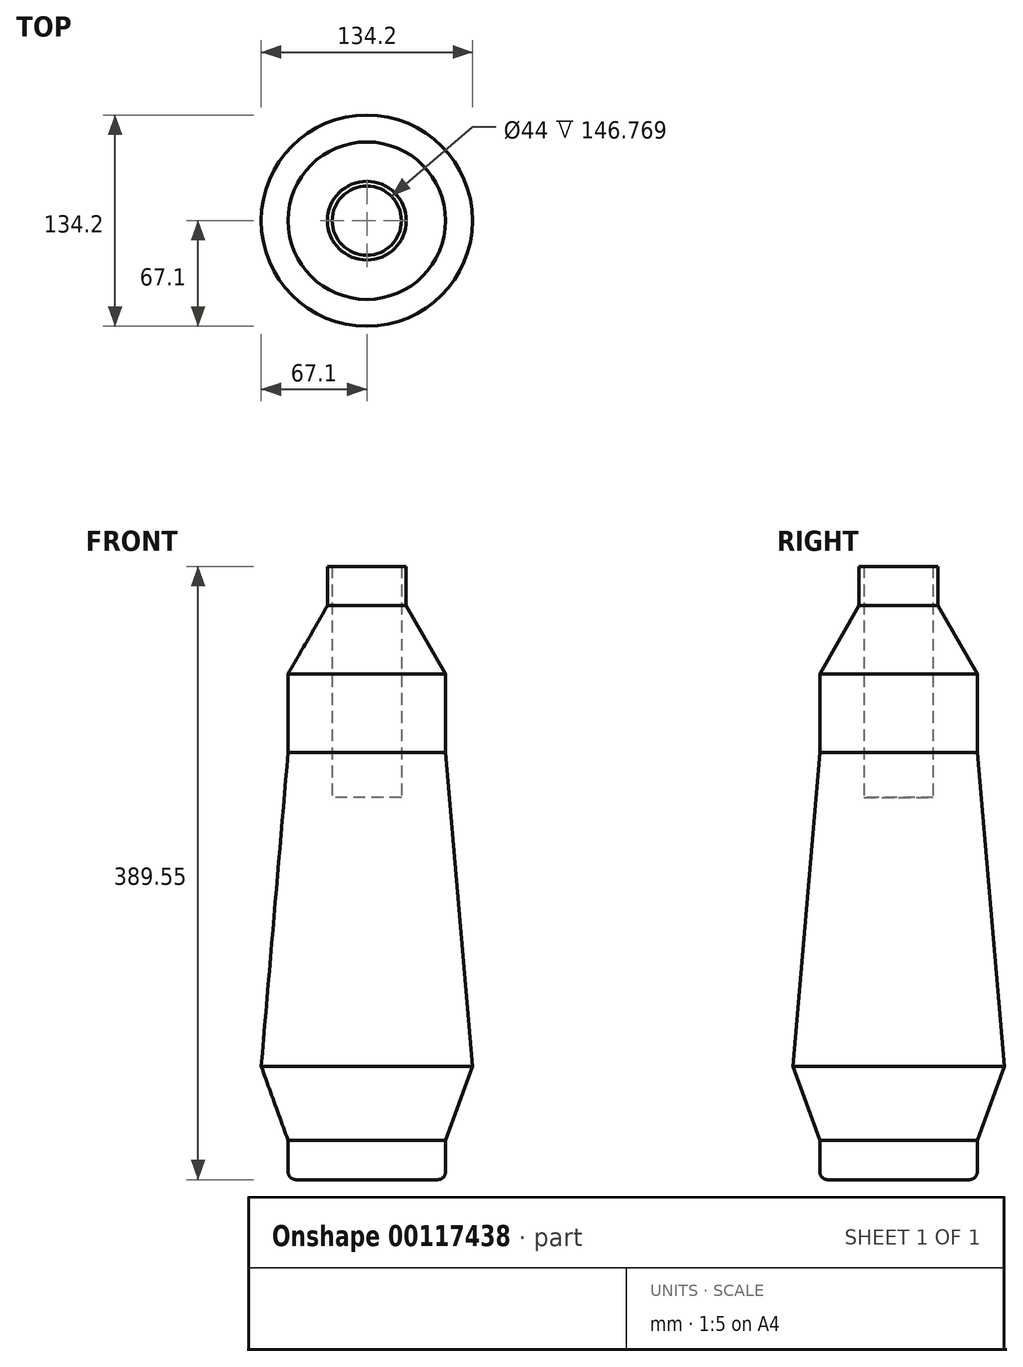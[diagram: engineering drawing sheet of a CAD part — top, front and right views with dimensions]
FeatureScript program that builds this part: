
annotation { "Feature Type Name" : "Feature", "Feature Type Description" : "" }
export const myFeature = defineFeature(function(context is Context, id is Id, definition is map)
    precondition{}
    {
        {
            var Q0;
            Q0=qCreatedBy(makeId("Front.planeOp"),FACE);
            var sketch = newSketch(context, id + "F0", { "sketchPlane" : qUnion([Q0])});
            skLineSegment(sketch, "E0", {"start": v(0, -242.78) * mm, "end": v(45, -242.78) * mm});
            skLineSegment(sketch, "E1", {"start": v(50, -237.78) * mm, "end": v(50, -217.78) * mm});
            skLineSegment(sketch, "E2", {"start": v(50, -217.78) * mm, "end": v(67.1, -170.8) * mm});
            skLineSegment(sketch, "E3", {"start": v(67.1, -170.8) * mm, "end": v(50, 28.47) * mm});
            skLineSegment(sketch, "E4", {"start": v(50, 28.47) * mm, "end": v(50, 78.47) * mm});
            skPoint(sketch, "E5.endSnap0", {"position": v(25, -242.78) * mm});
            skLineSegment(sketch, "E6", {"start": v(50, 78.47) * mm, "end": v(25, 121.77) * mm});
            skLineSegment(sketch, "E7", {"start": v(25, 121.77) * mm, "end": v(25, 146.77) * mm});
            skPoint(sketch, "E8.visualSharp", {"position": v(50, -242.78) * mm});
            skArc(sketch, "E8.filletArc", {"start": v(45, -242.78) * mm, "mid": v(48.54, -241.32) * mm, "end": v(50, -237.78) * mm});
            skLineSegment(sketch, "E9", {"start": v(0, -242.78) * mm, "end": v(0, 121.77) * mm});
            skLineSegment(sketch, "E10", {"start": v(0, -242.78) * mm, "end": v(0, 146.77) * mm});
            skLineSegment(sketch, "E11", {"start": v(25, 146.77) * mm, "end": v(21.86, 146.77) * mm});
            skLineSegment(sketch, "E12", {"start": v(21.86, 146.77) * mm, "end": v(21.86, 121.77) * mm});
            skLineSegment(sketch, "E13", {"start": v(21.86, 121.77) * mm, "end": v(0, 121.77) * mm});
            skLineSegment(sketch, "E14", {"start": v(0, 146.77) * mm, "end": v(21.86, 146.77) * mm});
            skSolve(sketch);
        }
        {
            var Q0;
            {var subQ0=sQuery(id+"F0.wireOp",EDGE,"E0");Q0=makeQuery(id+"F0.imprint","IMPRINT",FACE,{"disambiguationData":[TD([[makeQuery(id+"F0.imprint","IMPRINT",EDGE,{"derivedFrom":subQ0}),1.0]])]});}
            var Q1;
            Q1=sQuery(id+"F0.wireOp",EDGE,"E10");
            revolve(context, id + "F1", {"entities" : qUnion([Q0]), "axis" : qUnion([Q1]), "revolveType" : RevolveType.FULL});
        }
        {
            var Q0;
            Q0=qCreatedBy(makeId("Top.planeOp"),FACE);
            var sketch = newSketch(context, id + "F2", { "sketchPlane" : qUnion([Q0])});
            skCircle(sketch, "E15", {"center": v(0, 0) * mm, "radius": 22 * mm});
            skSolve(sketch);
        }
        {
            var Q0;
            Q0 = qSketchRegion(id + "F2", true);
            extrude(context, id + "F3", {"entities" : qUnion([Q0]), "operationType" : NewBodyOperationType.REMOVE, "depth" : 196.67 * mm});
        }
    });
